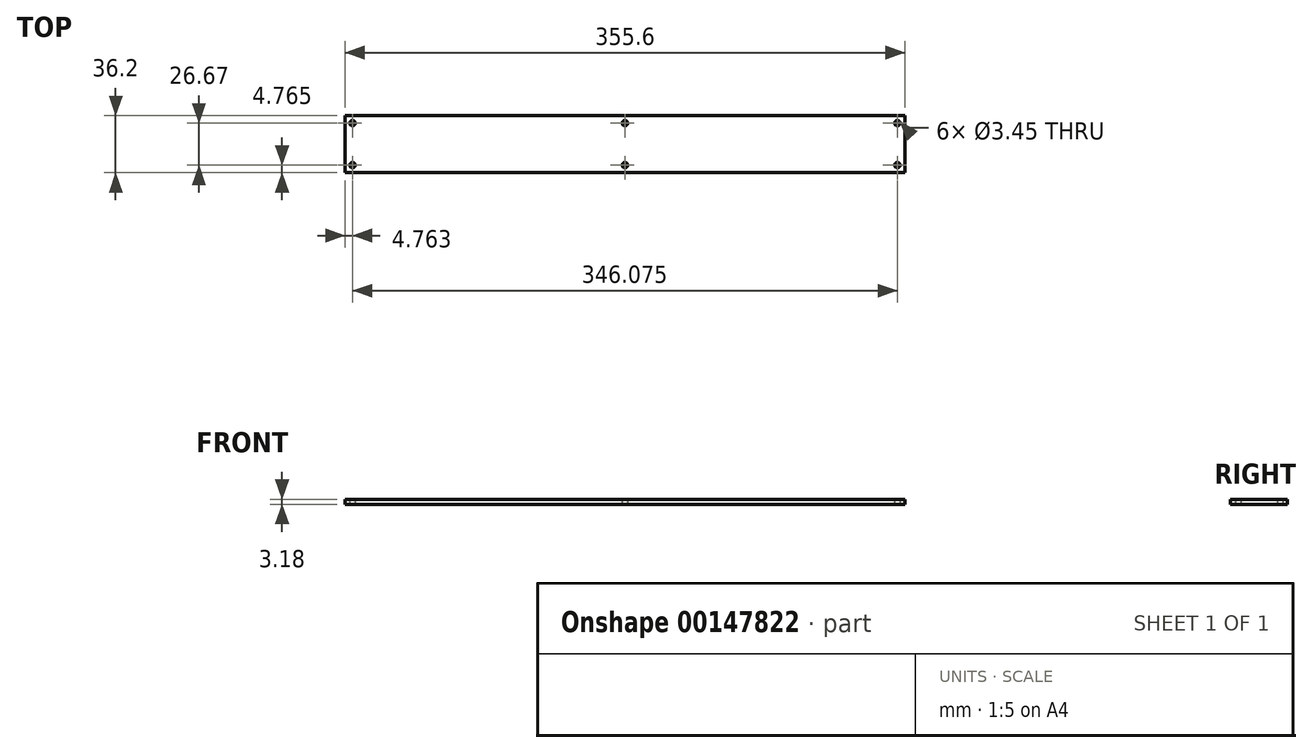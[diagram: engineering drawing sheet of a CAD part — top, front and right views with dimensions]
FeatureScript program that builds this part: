
annotation { "Feature Type Name" : "Feature", "Feature Type Description" : "" }
export const myFeature = defineFeature(function(context is Context, id is Id, definition is map)
    precondition{}
    {
        {
            var Q0;
            Q0=qCreatedBy(makeId("Top.planeOp"),FACE);
            var sketch = newSketch(context, id + "F0", { "sketchPlane" : qUnion([Q0])});
            skLineSegment(sketch, "E0.bottom", {"start": v(177.8, -18.1) * mm, "end": v(-177.8, -18.1) * mm});
            skLineSegment(sketch, "E0.top", {"start": v(177.8, 18.1) * mm, "end": v(-177.8, 18.1) * mm});
            skLineSegment(sketch, "E0.left", {"start": v(177.8, -18.1) * mm, "end": v(177.8, 18.1) * mm});
            skLineSegment(sketch, "E0.right", {"start": v(-177.8, -18.1) * mm, "end": v(-177.8, 18.1) * mm});
            skPoint(sketch, "E0.middle", {"position": v(0, 0) * mm});
            skLineSegment(sketch, "E1.bottom", {"start": v(173.04, -13.33) * mm, "end": v(-173.04, -13.34) * mm, "construction": true});
            skLineSegment(sketch, "E1.top", {"start": v(173.04, 13.34) * mm, "end": v(-173.04, 13.33) * mm, "construction": true});
            skLineSegment(sketch, "E1.left", {"start": v(173.04, -13.33) * mm, "end": v(173.04, 13.34) * mm, "construction": true});
            skLineSegment(sketch, "E1.right", {"start": v(-173.04, -13.34) * mm, "end": v(-173.04, 13.33) * mm, "construction": true});
            skLineSegment(sketch, "E2", {"start": v(-173.04, -13.34) * mm, "end": v(-173.04, -18.1) * mm, "construction": true});
            skLineSegment(sketch, "E3", {"start": v(-173.04, -13.34) * mm, "end": v(-177.8, -13.34) * mm, "construction": true});
            skCircle(sketch, "E4", {"center": v(-173.04, 13.33) * mm, "radius": 1.73 * mm});
            skCircle(sketch, "E5", {"center": v(-173.04, -13.34) * mm, "radius": 1.73 * mm});
            skCircle(sketch, "E6", {"center": v(173.04, -13.33) * mm, "radius": 1.73 * mm});
            skCircle(sketch, "E7", {"center": v(173.04, 13.34) * mm, "radius": 1.73 * mm});
            skCircle(sketch, "E8", {"center": v(0, 13.34) * mm, "radius": 1.73 * mm});
            skCircle(sketch, "E9", {"center": v(0, -13.34) * mm, "radius": 1.73 * mm});
            skSolve(sketch);
        }
        {
            var Q0;
            Q0=qSketchRegion(id+"F0",true);
            extrude(context, id + "F1", {"entities" : qUnion([Q0]), "depth" : 3.17 * mm});
        }
    });
